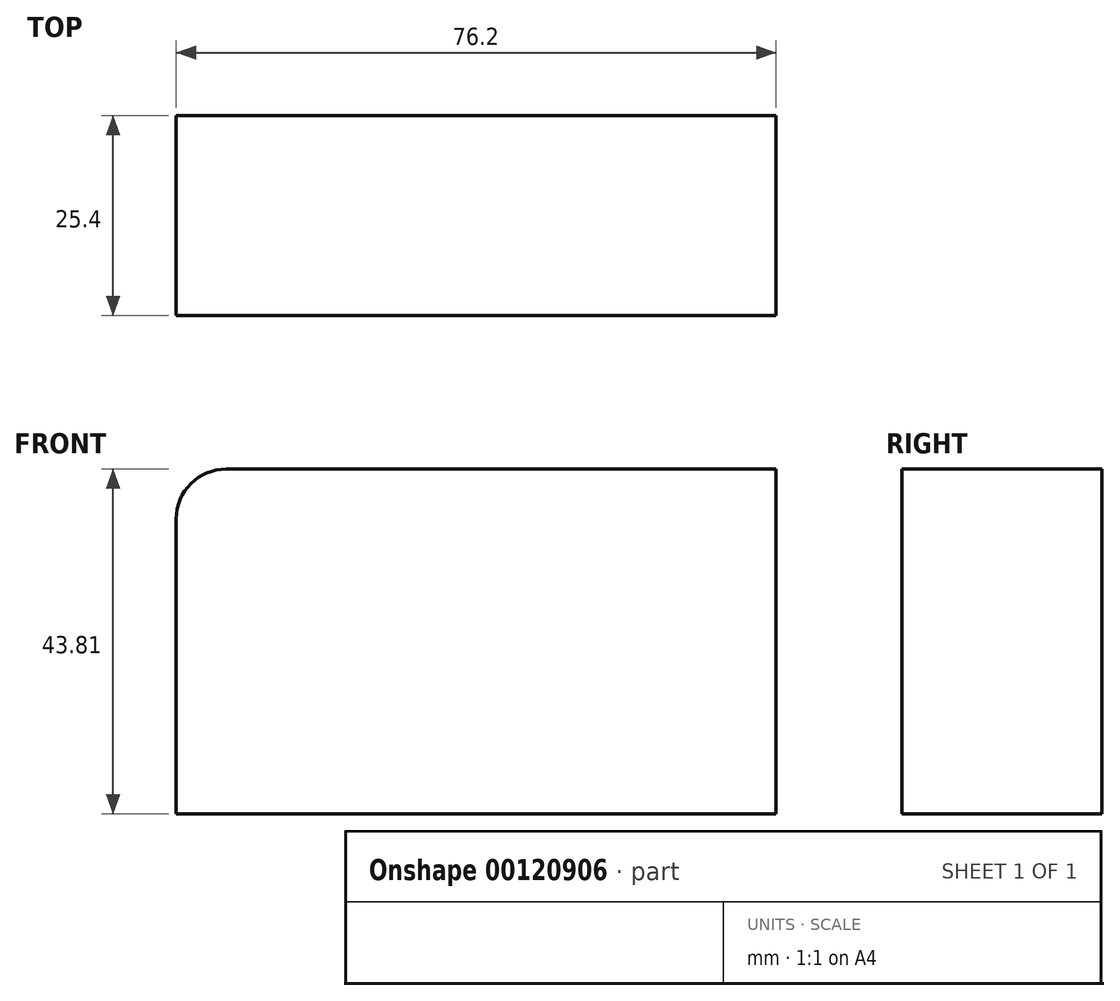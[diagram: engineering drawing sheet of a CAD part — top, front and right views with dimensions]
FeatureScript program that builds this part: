
annotation { "Feature Type Name" : "Feature", "Feature Type Description" : "" }
export const myFeature = defineFeature(function(context is Context, id is Id, definition is map)
    precondition{}
    {
        {
            var Q0;
            Q0=qCreatedBy(makeId("Front.planeOp"),FACE);
            var sketch = newSketch(context, id + "F0", { "sketchPlane" : qUnion([Q0])});
            skLineSegment(sketch, "E0.bottom", {"start": v(-34.89, 25.4) * mm, "end": v(34.96, 25.4) * mm});
            skLineSegment(sketch, "E0.top", {"start": v(-41.24, -18.4) * mm, "end": v(34.96, -18.4) * mm});
            skLineSegment(sketch, "E0.left", {"start": v(-41.24, 19.05) * mm, "end": v(-41.24, -18.4) * mm});
            skLineSegment(sketch, "E0.right", {"start": v(34.96, 25.4) * mm, "end": v(34.96, -18.4) * mm});
            skPoint(sketch, "E1.visualSharp", {"position": v(-41.24, 25.4) * mm});
            skArc(sketch, "E1.filletArc", {"start": v(-34.89, 25.4) * mm, "mid": v(-39.38, 23.54) * mm, "end": v(-41.24, 19.05) * mm});
            skSolve(sketch);
        }
        {
            var Q0;
            Q0=makeQuery(id+"F0.imprint","IMPRINT",FACE,{"disambiguationData":[TD([[makeQuery(id+"F0.imprint","IMPRINT",EDGE,{"derivedFrom":sQuery(id+"F0.wireOp",EDGE,"E0.bottom")}),-1.0]])]});
            extrude(context, id + "F1", {"entities" : qUnion([Q0]), "depth" : 25.4 * mm});
        }
    });
